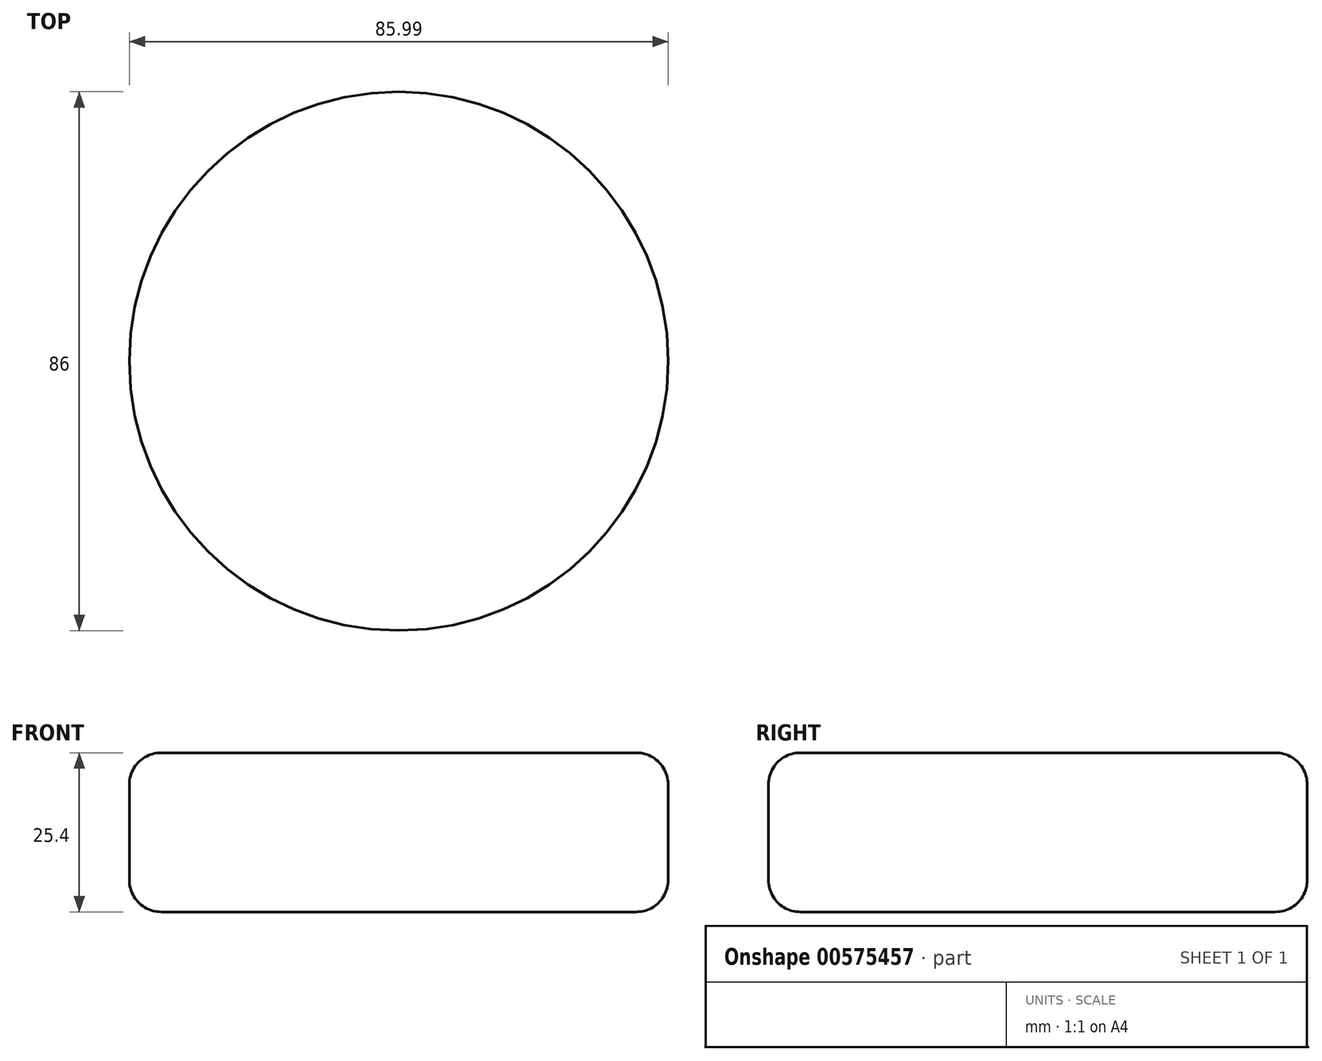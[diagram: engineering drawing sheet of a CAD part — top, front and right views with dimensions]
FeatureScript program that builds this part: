
annotation { "Feature Type Name" : "Feature", "Feature Type Description" : "" }
export const myFeature = defineFeature(function(context is Context, id is Id, definition is map)
    precondition{}
    {
        {
            var Q0;
            Q0=qCreatedBy(makeId("Top.planeOp"),FACE);
            var sketch = newSketch(context, id + "F0", { "sketchPlane" : qUnion([Q0])});
            skCircle(sketch, "E0", {"center": v(-24.47, 9.14) * mm, "radius": 43 * mm});
            skSolve(sketch);
        }
        {
            var Q0;
            Q0=makeQuery(id+"F0.imprint","IMPRINT",FACE,{"disambiguationData":[TD([[makeQuery(id+"F0.imprint","IMPRINT",EDGE,{"derivedFrom":sQuery(id+"F0.wireOp",EDGE,"E0")}),1.0]])]});
            extrude(context, id + "F1", {"entities" : qUnion([Q0]), "depth" : 25.4 * mm, "offsetDistance" : 25.4 * mm});
        }
        {
            var Q0;
            Q0=makeQuery(id+"F1.opExtrude","SWEPT_FACE",FACE,{"disambiguationData":[OSD([sQuery(id+"F0.wireOp",EDGE,"E0")])]});
            fillet(context, id + "F2", {"entities" : qUnion([Q0]), "radius" : 5.08 * mm, "tangentPropagation" : true, "allowEdgeOverflow" : false});
        }
    });
